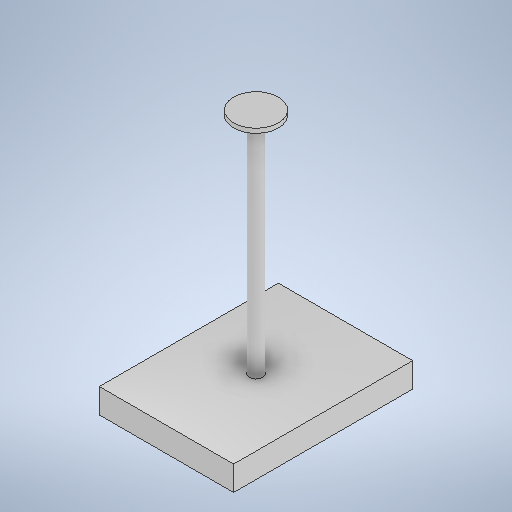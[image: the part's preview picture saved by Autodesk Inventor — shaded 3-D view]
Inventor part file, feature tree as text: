
AUTODESK INVENTOR PART (.ipt)
format: ipt  version: 2025.2 (Build 292293000, 293)  size: 285,696 bytes
history: native  units: mm
features: extrude x4, sketch x4, projected_geometry x1
ambient origin geometry x8: Origin, YZ Plane, XZ Plane, XY Plane, X Axis, Y Axis, Z Axis, Center Point
bodies: Solid1 (feature_tree)
feature tree (9):
  extrude  "Extrusion1"  Depth=600.0mm
  extrude  "Extrusion2"  Depth=50.0mm
  extrude  "Extrusion3"  Depth=50.0mm
  extrude  "Extrusion4"  Depth=50.0mm
  sketch  "Sketch1"  dims[d0=800.0mm d1=600.0mm]
  sketch  "Sketch2"  dims[d2=50.0mm d3=50.0mm]
  sketch  "Sketch3"  dims[d4=50.0mm d5=50.0mm]
  projected_geometry  "Projected Loop1"
  sketch  "Sketch4"  dims[d6=100.0mm d7=0.0mm d8=50.0mm d9=10.0mm d10=0.0mm d11=60.0mm d12=1000.0mm d13=0.0mm d14=200.0mm d15=20.0mm d16=0.0mm]
